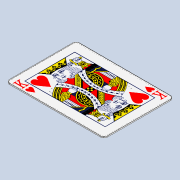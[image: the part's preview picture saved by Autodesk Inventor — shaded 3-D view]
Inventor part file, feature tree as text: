
AUTODESK INVENTOR PART (.ipt)
format: ipt  version: 2021 (Build 250183000, 183)  size: 1,413,120 bytes
history: native  units: mm
features: sketch x6, fillet x5, extrude x4, other x4, plane x2
ambient origin geometry x8: Origin, YZ Plane, XZ Plane, XY Plane, X Axis, Y Axis, Z Axis, Center Point
bodies: Solid1 (feature_tree)
feature tree (21):
  extrude  "Extrusion1"  Depth=88.9mm
  extrude  "Extrusion2"  Depth=0.8mm TaperAngle=0.0deg
  extrude  "Extrusion3"  Depth=10.0mm
  fillet  "Fillet3"  Radius=30.0mm
  fillet  "Fillet4"  Radius=30.0mm
  fillet  "Fillet5"  Radius=10.0mm
  extrude  "Extrusion5"  Depth=0.5mm
  plane  "Work Plane1"
  other  "Decal1"
  fillet  "Fillet6"  Radius=0.5mm
  fillet  "Fillet7"  Radius=0.3mm
  plane  "Work Plane2"
  other  "Decal2"
  sketch  "Sketch1"  dims[d0=63.5mm d1=88.9mm]
  sketch  "Sketch2"  dims[d2=1.0mm d3=0.0mm d6=0.8mm d7=0.0mm]
  sketch  "Sketch3"  dims[d8=10.0mm d9=10.0mm d10=30.0mm d11=30.0mm d12=10.0mm]
  sketch  "Sketch5"  dims[d13=0.6mm d14=0.0mm d15=0.5mm d16=0.5mm d17=0.3mm]
  sketch  "Sketch6"  dims[d24=87.0mm d25=0.0mm]
  other  "Image1"
  sketch  "Sketch7"  dims[d26=20.0mm d32=3.0mm d33=3.0mm d35=5.0mm]
  other  "Image2"
